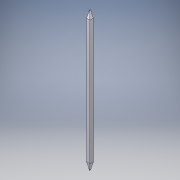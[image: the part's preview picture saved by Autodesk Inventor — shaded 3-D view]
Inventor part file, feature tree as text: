
AUTODESK INVENTOR PART (.ipt)
format: ipt  version: 2018 (Build 220112000, 112)  size: 149,504 bytes
history: native  units: in
note: dims shown in document units (in); Inventor stores cm internally (conversion verified against a paired STEP export)
features: plane x4, sketch x3, extrude x2, loft x1, hole x1, mirror x1, other x1
ambient origin geometry x8: Origin, YZ Plane, XZ Plane, XY Plane, X Axis, Y Axis, Z Axis, Center Point
bodies: Body1 (feature_tree)
feature tree (13):
  extrude  "Extrusion3"  Depth=36.0in
  plane  "Work Plane4"
  loft  "Loft3"
  plane  "Work Plane5"
  extrude  "Extrusion4"  Depth=12.0in
  hole  "Hole1"  [1 undecoded]
  mirror  "Mirror1"
  sketch  "Sketch5"  dims[d26=36.0in d27=36.0in]
  sketch  "Sketch6"  dims[d28=1320.0in d29=0.0in d30=60.0in]
  other  "Edges3"
  sketch  "Sketch7"  dims[d31=12.0in d32=12.0in d33=12.0in d34=12.0in d35=0.0in d36=90.0deg d37=0.0in d38=90.0deg d39=90.0deg d40=12.0in d41=1320.0in d42=0.0in d43=1.0in d44=1.0in d45=3.0in d46=0.75in d47=0.375in d48=0.25in d49=0.5635in d50=1.0in d51=0.8108in]
  plane  "Work Plane6"
  plane  "Work Plane7"
note: 1 required parameter value undecoded (feature->parameter linkage not recoverable at this tier; creation-order binding heuristic only, values carry confidence <= 0.55)
